# Revit family: JOMA_Takåsfäste Vänster
name_source: partatom
category: Structural Connections
revit_build: Autodesk Revit Structure 2012 (Build: 20110309_2315(x64)
units: mm (PartAtom-declared; Revit-internal decimal feet)

## types (6) — shared parameters
Default Elevation = 1219 mm
Länk Joma Dimensioneringsverktyg = http://www.joma.se
Material = Varmförzinkad stålplåt

## per-type parameters (varying)
| type | A | B | Typ 170 | Typ 210 | Typ 250 | Typ 290 | Typ 330 | Typ 370 | Vikt |
| 580170V | 170 mm | 50 mm | Yes | No | No | No | No | No | 0,10 |
| 580210V | 210 mm | 50 mm | No | Yes | No | No | No | No | 0,14 |
| 580250V | 250 mm | 50 mm | No | No | Yes | No | No | No | 0,18 |
| 580290V | 290 mm | 40 mm  [stored 0.131234 ft] | No | No | No | Yes | No | No | 0,22 |
| 580330V | 330 mm | 40 mm  [stored 0.131234 ft] | No | No | No | No | Yes | No | 0,26 |
| 580370V | 370 mm  [stored 1.21391 ft] | 40 mm  [stored 0.131234 ft] | No | No | No | No | No | Yes | 0,30 |

note: [stored X ft] marks values corroborated as IEEE doubles in the binary element streams (Revit-internal decimal feet)

## geometry (parser evidence)
native form markers: Sweep x2
no freeform markers — native parametric forms only
